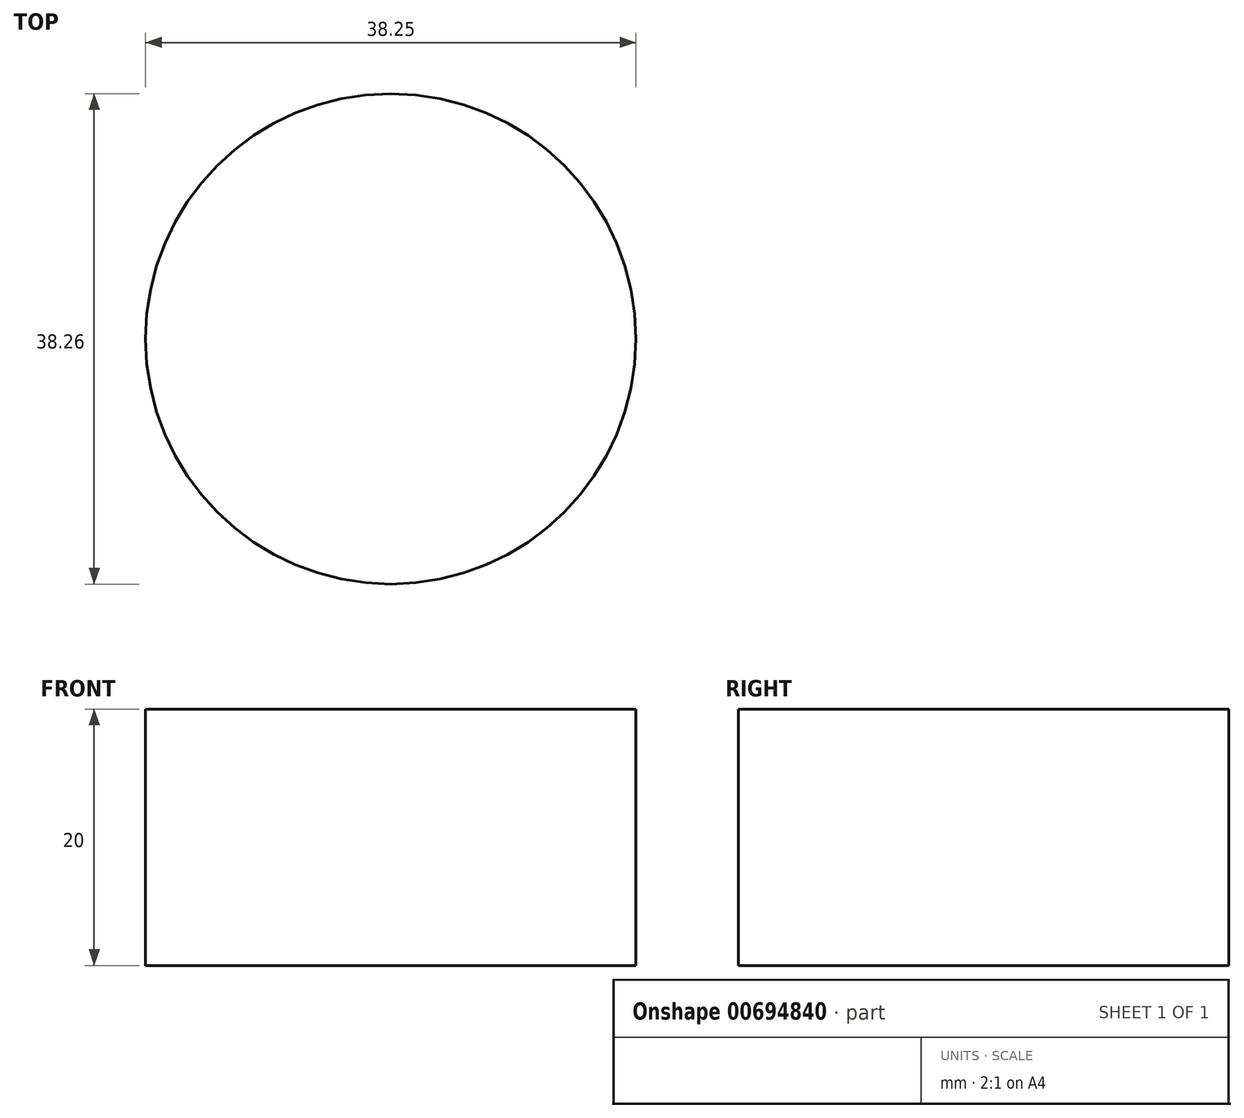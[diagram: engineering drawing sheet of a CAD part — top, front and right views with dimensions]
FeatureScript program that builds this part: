
annotation { "Feature Type Name" : "Feature", "Feature Type Description" : "" }
export const myFeature = defineFeature(function(context is Context, id is Id, definition is map)
    precondition{}
    {
        {
            var Q0;
            Q0=qCreatedBy(makeId("Top.planeOp"),FACE);
            var sketch = newSketch(context, id + "F0", { "sketchPlane" : qUnion([Q0])});
            skCircle(sketch, "E0", {"center": v(19.13, 0) * mm, "radius": 19.13 * mm});
            skCircle(sketch, "E1", {"center": v(18.07, 19.1) * mm, "radius": 19.13 * mm, "construction": true});
            skSolve(sketch);
        }
        {
            var Q0;
            Q0=makeQuery(id+"F0.imprint","IMPRINT",FACE,{"disambiguationData":[TD([[makeQuery(id+"F0.imprint","IMPRINT",EDGE,{"derivedFrom":sQuery(id+"F0.wireOp",EDGE,"E0")}),1.0]])]});
            extrude(context, id + "F1", {"entities" : qUnion([Q0]), "depth" : 20 * mm, "offsetDistance" : 25.4 * mm});
        }
    });
